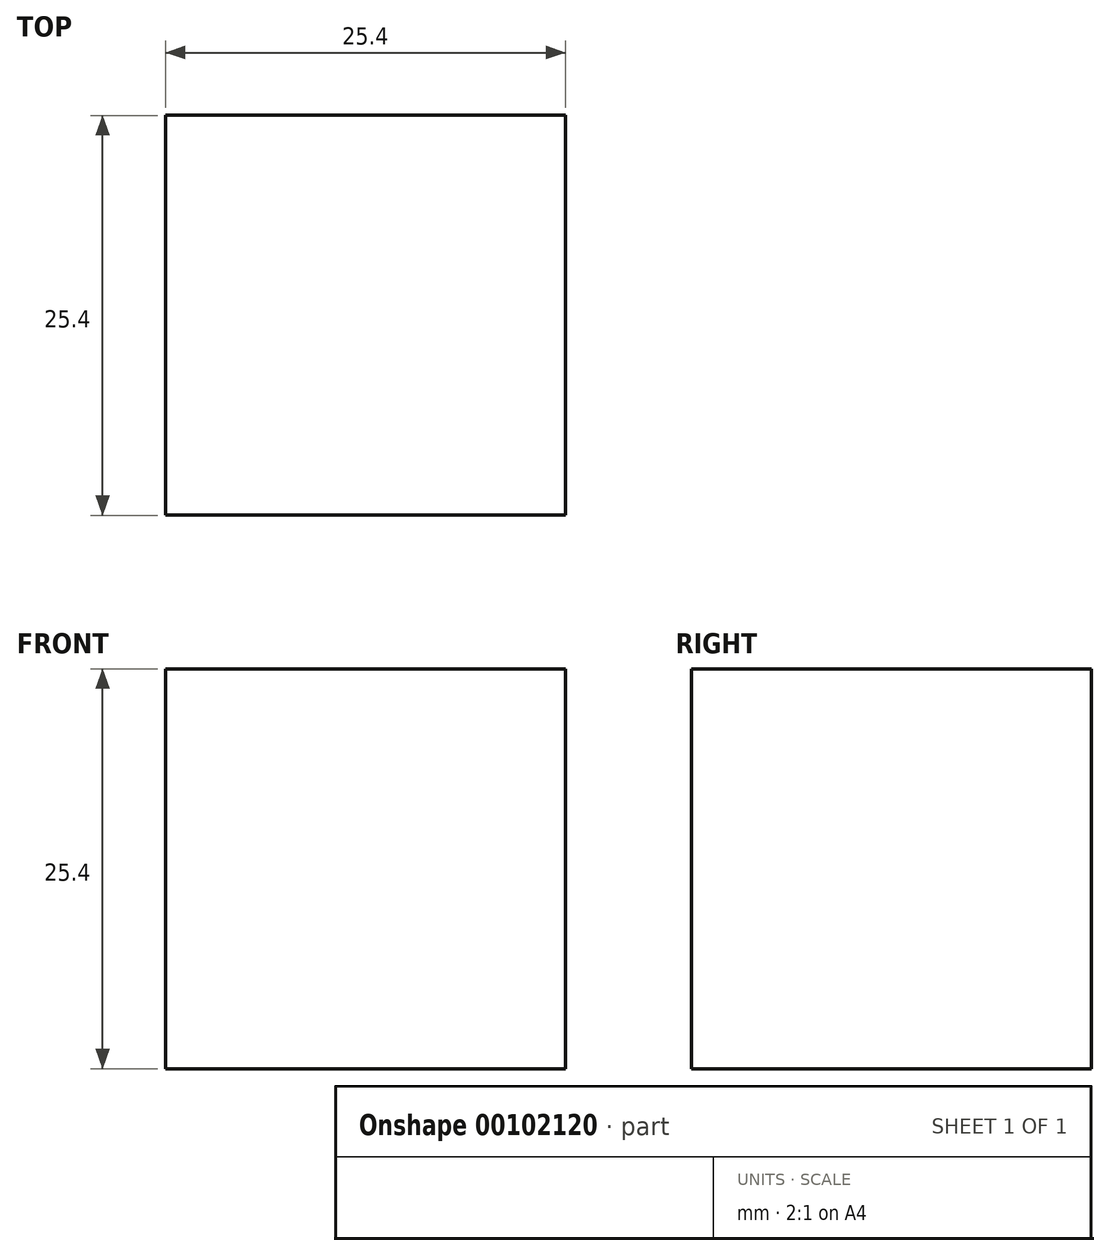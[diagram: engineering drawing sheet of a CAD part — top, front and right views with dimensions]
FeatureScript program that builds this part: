
annotation { "Feature Type Name" : "Feature", "Feature Type Description" : "" }
export const myFeature = defineFeature(function(context is Context, id is Id, definition is map)
    precondition{}
    {
        {
            var Q0;
            Q0=qCreatedBy(makeId("Top.planeOp"),FACE);
            var sketch = newSketch(context, id + "F0", { "sketchPlane" : qUnion([Q0])});
            skLineSegment(sketch, "E0.bottom", {"start": v(-11.32, 17.04) * mm, "end": v(14.08, 17.04) * mm});
            skLineSegment(sketch, "E0.top", {"start": v(-11.32, -8.36) * mm, "end": v(14.08, -8.36) * mm});
            skLineSegment(sketch, "E0.left", {"start": v(-11.32, 17.04) * mm, "end": v(-11.32, -8.36) * mm});
            skLineSegment(sketch, "E0.right", {"start": v(14.08, 17.04) * mm, "end": v(14.08, -8.36) * mm});
            skSolve(sketch);
        }
        {
            var Q0;
            Q0=makeQuery(id+"F0.imprint","IMPRINT",FACE,{"disambiguationData":[TD([[makeQuery(id+"F0.imprint","IMPRINT",EDGE,{"derivedFrom":sQuery(id+"F0.wireOp",EDGE,"E0.bottom")}),-1.0]])]});
            extrude(context, id + "F1", {"entities" : qUnion([Q0]), "depth" : 25.4 * mm});
        }
    });
